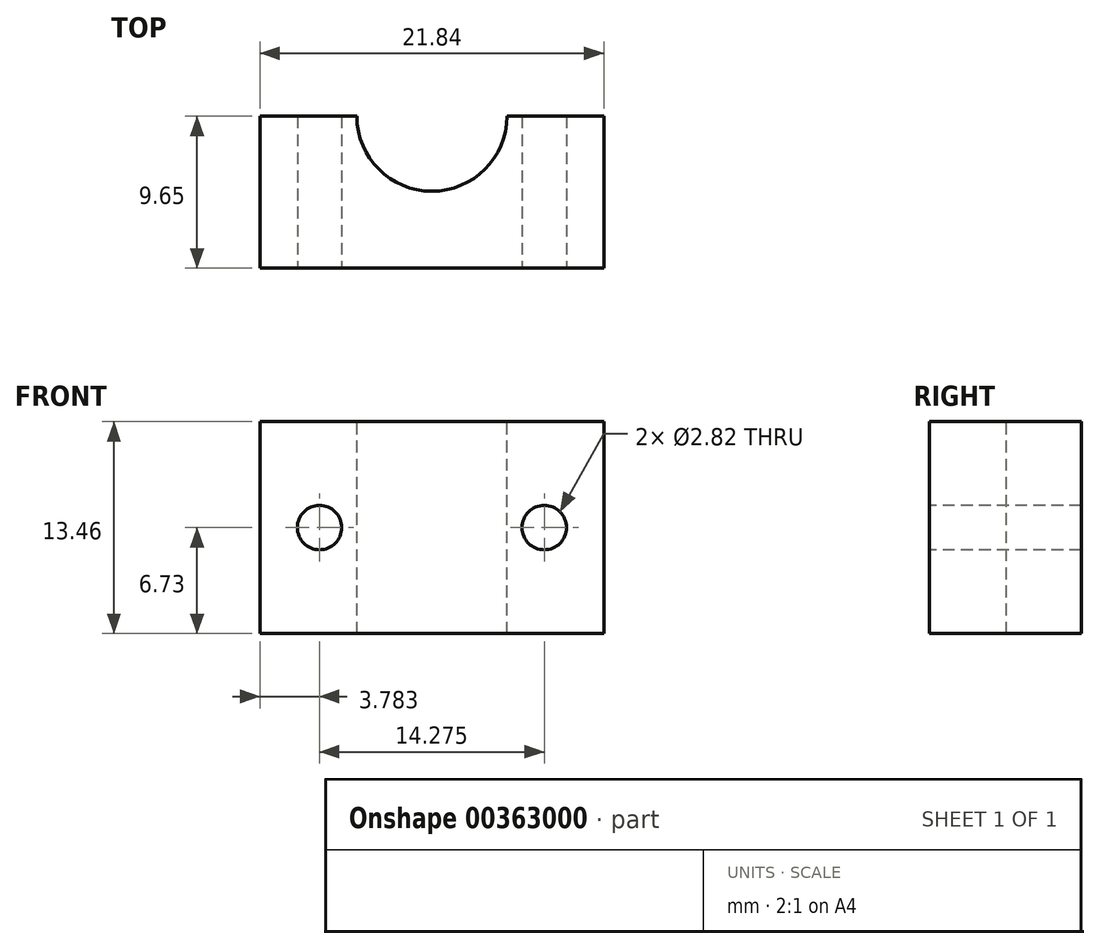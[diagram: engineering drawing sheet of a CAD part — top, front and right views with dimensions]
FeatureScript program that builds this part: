
annotation { "Feature Type Name" : "Feature", "Feature Type Description" : "" }
export const myFeature = defineFeature(function(context is Context, id is Id, definition is map)
    precondition{}
    {
        {
            var Q0;
            Q0=qCreatedBy(makeId("Front.planeOp"),FACE);
            var sketch = newSketch(context, id + "F0", { "sketchPlane" : qUnion([Q0])});
            skLineSegment(sketch, "E0.bottom", {"start": v(10.92, 6.73) * mm, "end": v(-10.92, 6.73) * mm});
            skLineSegment(sketch, "E0.top", {"start": v(10.92, -6.73) * mm, "end": v(-10.92, -6.73) * mm});
            skLineSegment(sketch, "E0.left", {"start": v(10.92, 6.73) * mm, "end": v(10.92, -6.73) * mm});
            skLineSegment(sketch, "E0.right", {"start": v(-10.92, 6.73) * mm, "end": v(-10.92, -6.73) * mm});
            skPoint(sketch, "E0.middle", {"position": v(0, 0) * mm});
            skSolve(sketch);
        }
        {
            var Q0;
            Q0=makeQuery(id+"F0.imprint","IMPRINT",FACE,{"disambiguationData":[TD([[makeQuery(id+"F0.imprint","IMPRINT",EDGE,{"derivedFrom":sQuery(id+"F0.wireOp",EDGE,"E0.bottom")}),1.0]])]});
            extrude(context, id + "F1", {"entities" : qUnion([Q0]), "depth" : 9.65 * mm});
        }
        {
            var Q0;
            Q0=makeQuery(id+"F1.opExtrude","CAP_FACE",FACE,{"disambiguationData":[OSD([sQuery(id+"F0.wireOp",EDGE,"E0.bottom"),sQuery(id+"F0.wireOp",EDGE,"E0.top"),sQuery(id+"F0.wireOp",EDGE,"E0.left"),sQuery(id+"F0.wireOp",EDGE,"E0.right")])],"isStart":false});
            var sketch = newSketch(context, id + "F2", { "sketchPlane" : qUnion([Q0])});
            skPoint(sketch, "E1", {"position": v(-7.14, 0) * mm});
            skPoint(sketch, "E2", {"position": v(7.14, 0) * mm});
            skSolve(sketch);
        }
        {
            var Q0;
            Q0=sQuery(id+"F2.wireOp",VERTEX,"E1");
            var Q1;
            Q1=sQuery(id+"F2.wireOp",VERTEX,"E2");
            var Q2;
            Q2=makeQuery(id+"F1.opExtrude","SWEPT_BODY",BODY,{"disambiguationData":[OSD([sQuery(id+"F0.wireOp",EDGE,"E0.bottom"),sQuery(id+"F0.wireOp",EDGE,"E0.top"),sQuery(id+"F0.wireOp",EDGE,"E0.left"),sQuery(id+"F0.wireOp",EDGE,"E0.right")])]});
            hole(context, id + "F3", {"style" : HoleStyle.SIMPLE, "endStyle" : HoleEndStyle.THROUGH, "standardTappedOrClearance" : lookupTablePath({ "standard" : "ANSI", "size" : "#34 (0.1)", "type" : "Drilled" }), "standardBlindInLast" : lookupTablePath({ "standard" : "ANSI", "size" : "#34", "type" : "Drilled" }), "holeDiameter" : 2.82 * mm, "tappedDepth" : 4.57 * mm, "tapClearance" : 3, "locations" : qUnion([Q0, Q1]), "scope" : qUnion([Q2])});
        }
        {
            var Q0;
            Q0=makeQuery(id+"F1.opExtrude","SWEPT_FACE",FACE,{"disambiguationData":[OSD([sQuery(id+"F0.wireOp",EDGE,"E0.bottom")])]});
            var sketch = newSketch(context, id + "F4", { "sketchPlane" : qUnion([Q0])});
            skCircle(sketch, "E3", {"center": v(0, 0) * mm, "radius": 4.76 * mm});
            skSolve(sketch);
        }
        {
            var Q0;
            {var subQ0=sQuery(id+"F4.wireOp",EDGE,"E3");var subQ1=makeQuery(id+"F1.opExtrude","CAP_EDGE",EDGE,{"disambiguationData":[OSD([sQuery(id+"F0.wireOp",EDGE,"E0.bottom")])],"isStart":true});var subQ2=makeQuery(id+"F4.imprint","INTERSECT",VERTEX,{"disambiguationData":[OD(0.0)],"derivedFrom":[subQ1,subQ0]});Q0=makeQuery(id+"F4.imprint","IMPRINT",FACE,{"disambiguationData":[TD([[makeQuery(id+"F4.imprint","IMPRINT",EDGE,{"disambiguationData":[TD([[subQ2,1.0]])],"derivedFrom":subQ0}),1.0]])]});}
            extrude(context, id + "F5", {"entities" : qUnion([Q0]), "operationType" : NewBodyOperationType.REMOVE, "endBound" : BoundingType.THROUGH_ALL, "oppositeDirection" : true, "depth" : 25.4 * mm});
        }
    });
